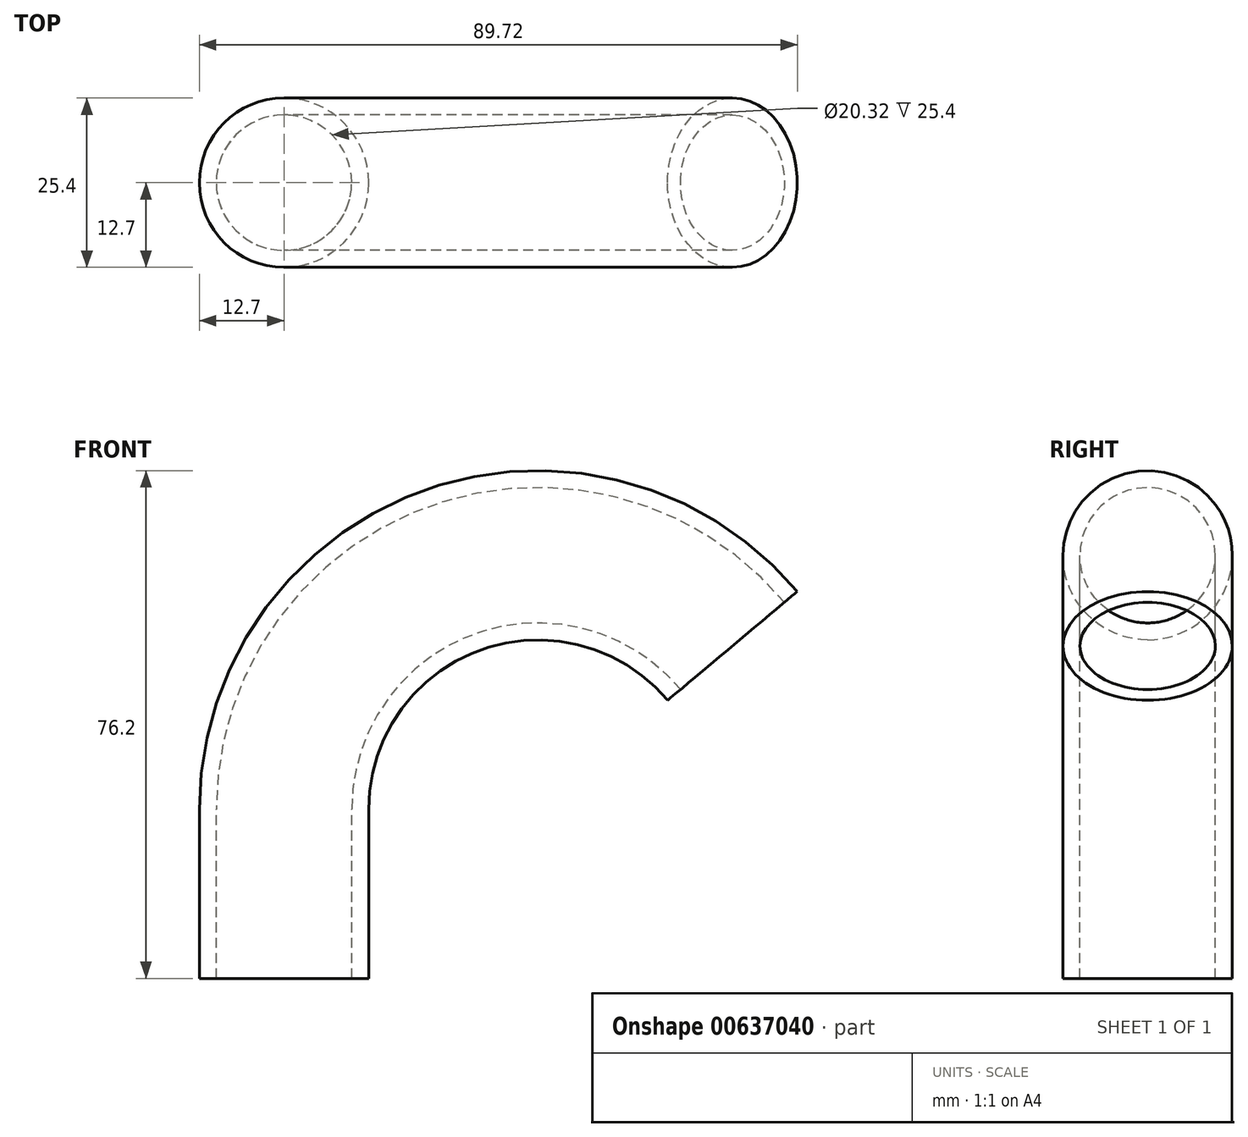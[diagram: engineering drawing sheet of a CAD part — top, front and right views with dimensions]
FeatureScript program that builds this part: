
annotation { "Feature Type Name" : "Feature", "Feature Type Description" : "" }
export const myFeature = defineFeature(function(context is Context, id is Id, definition is map)
    precondition{}
    {
        {
            var Q0;
            Q0=qCreatedBy(makeId("Top.planeOp"),FACE);
            var sketch = newSketch(context, id + "F0", { "sketchPlane" : qUnion([Q0])});
            skCircle(sketch, "E0", {"center": v(0, 0) * mm, "radius": 12.7 * mm});
            skLineSegment(sketch, "E1", {"start": v(38.1, 29.6) * mm, "end": v(38.1, -36.84) * mm});
            skSolve(sketch);
        }
        {
            var Q0;
            Q0=makeQuery(id+"F0.imprint","IMPRINT",FACE,{"disambiguationData":[TD([[makeQuery(id+"F0.imprint","IMPRINT",EDGE,{"derivedFrom":sQuery(id+"F0.wireOp",EDGE,"E0")}),1.0]])]});
            var Q1;
            Q1=sQuery(id+"F0.wireOp",EDGE,"E1");
            revolve(context, id + "F1", {"entities" : qUnion([Q0]), "axis" : qUnion([Q1]), "revolveType" : RevolveType.ONE_DIRECTION, "oppositeDirection" : true, "angle" : 140 * degree});
        }
        {
            var Q0;
            Q0=makeQuery(id+"F1.opRevolve","CAP_FACE",FACE,{"disambiguationData":[OSD([sQuery(id+"F0.wireOp",EDGE,"E0")])],"isStart":true});
            extrude(context, id + "F2", {"entities" : qUnion([Q0]), "operationType" : NewBodyOperationType.ADD, "depth" : 25.4 * mm, "offsetDistance" : 25.4 * mm});
        }
        {
            var Q0;
            Q0=makeQuery(id+"F2.opExtrude","CAP_FACE",FACE,{"disambiguationData":[OSD([sQuery(id+"F0.wireOp",EDGE,"E0")])],"isStart":false});
            var Q1;
            Q1=makeQuery(id+"F1.opRevolve","CAP_FACE",FACE,{"disambiguationData":[OSD([sQuery(id+"F0.wireOp",EDGE,"E0")])],"isStart":false});
            shell(context, id + "F3", {"entities" : qUnion([Q0, Q1]), "thickness" : 2.54 * mm});
        }
    });
